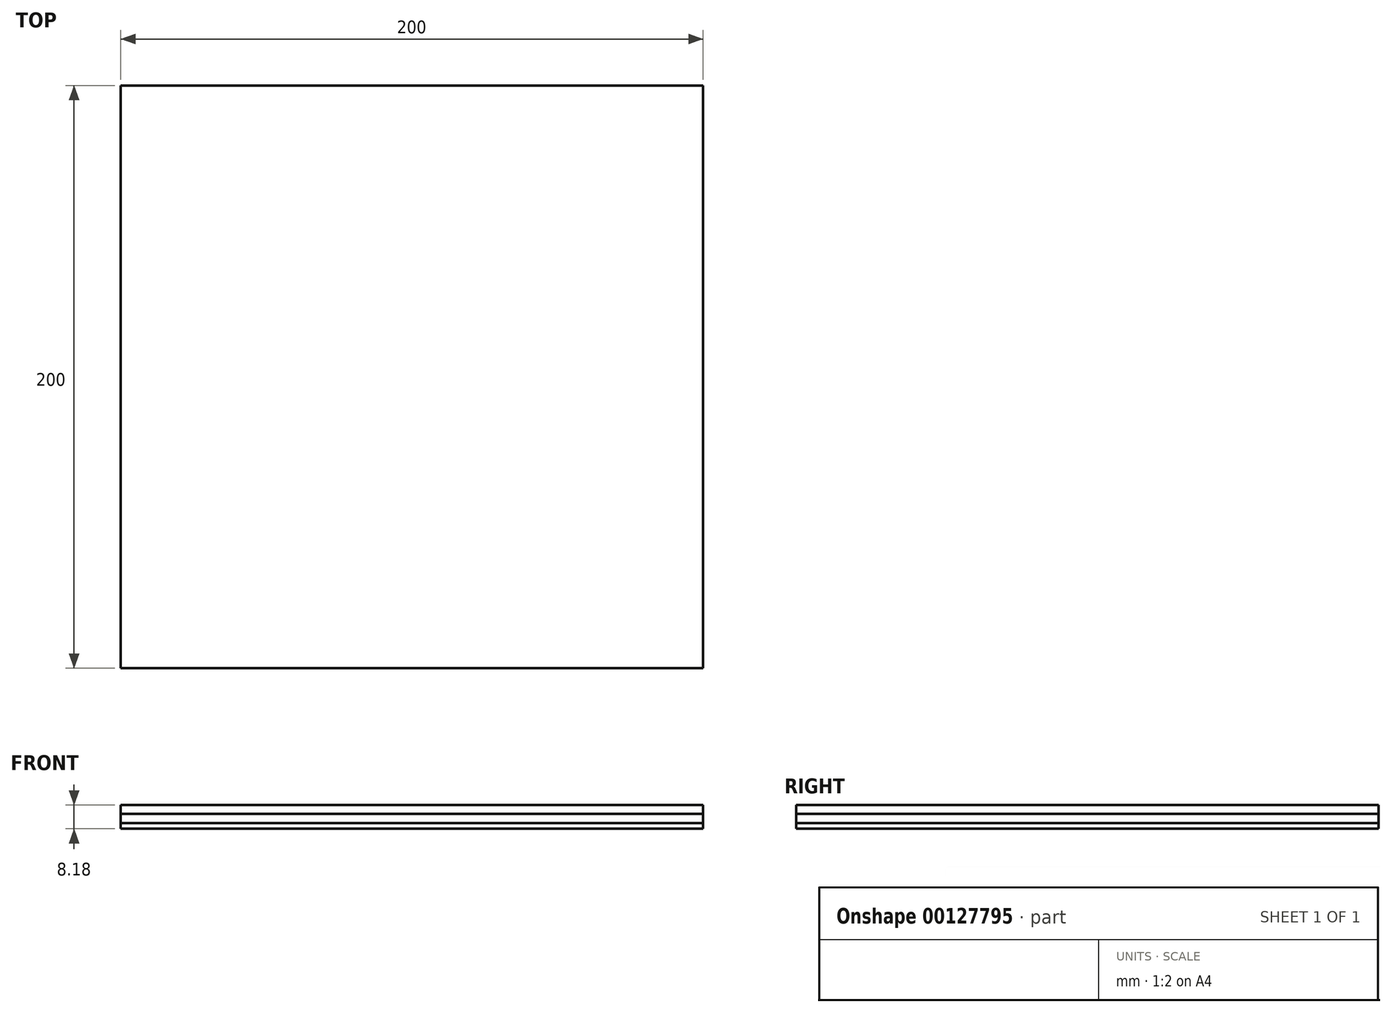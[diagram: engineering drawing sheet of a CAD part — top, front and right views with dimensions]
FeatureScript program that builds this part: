
annotation { "Feature Type Name" : "Feature", "Feature Type Description" : "" }
export const myFeature = defineFeature(function(context is Context, id is Id, definition is map)
    precondition{}
    {
        {
            var Q0;
            Q0=qCreatedBy(makeId("Top.planeOp"),FACE);
            var sketch = newSketch(context, id + "F0", { "sketchPlane" : qUnion([Q0])});
            skLineSegment(sketch, "E0.bottom", {"start": v(100, -100) * mm, "end": v(-100, -100) * mm});
            skLineSegment(sketch, "E0.top", {"start": v(100, 100) * mm, "end": v(-100, 100) * mm});
            skLineSegment(sketch, "E0.left", {"start": v(100, -100) * mm, "end": v(100, 100) * mm});
            skLineSegment(sketch, "E0.right", {"start": v(-100, -100) * mm, "end": v(-100, 100) * mm});
            skPoint(sketch, "E0.middle", {"position": v(0, 0) * mm});
            skSolve(sketch);
        }
        {
            var Q0;
            Q0 = qSketchRegion(id + "F0", true);
            extrude(context, id + "F1", {"entities" : qUnion([Q0]), "endBound" : BoundingType.SYMMETRIC, "depth" : 3.17 * mm});
        }
        {
            var Q0;
            Q0=makeQuery(id+"F1.opExtrude","CAP_FACE",FACE,{"disambiguationData":[OSD([sQuery(id+"F0.wireOp",EDGE,"E0.bottom"),sQuery(id+"F0.wireOp",EDGE,"E0.top"),sQuery(id+"F0.wireOp",EDGE,"E0.left"),sQuery(id+"F0.wireOp",EDGE,"E0.right")])],"isStart":false});
            var sketch = newSketch(context, id + "F2", { "sketchPlane" : qUnion([Q0])});
            skCircle(sketch, "E1", {"center": v(-90, -140) * mm, "radius": 2.5 * mm});
            skCircle(sketch, "E2", {"center": v(-90, 140) * mm, "radius": 2.5 * mm});
            skLineSegment(sketch, "E3", {"start": v(-46.85, 0) * mm, "end": v(0, 0) * mm, "construction": true});
            skLineSegment(sketch, "E4", {"start": v(0, 0) * mm, "end": v(0, 84.57) * mm, "construction": true});
            skCircle(sketch, "E5.MirrorC", {"center": v(90, 140) * mm, "radius": 2.5 * mm});
            skCircle(sketch, "E6.MirrorC", {"center": v(90, -140) * mm, "radius": 2.5 * mm});
            skSolve(sketch);
        }
        {
            var Q0;
            Q0 = qSketchRegion(id + "F2", true);
            extrude(context, id + "F3", {"entities" : qUnion([Q0]), "operationType" : NewBodyOperationType.REMOVE, "endBound" : BoundingType.THROUGH_ALL, "oppositeDirection" : true, "depth" : 25 * mm});
        }
        {
            var Q0;
            Q0=makeQuery(id+"F1.opExtrude","CAP_FACE",FACE,{"disambiguationData":[OSD([sQuery(id+"F0.wireOp",EDGE,"E0.bottom"),sQuery(id+"F0.wireOp",EDGE,"E0.top"),sQuery(id+"F0.wireOp",EDGE,"E0.left"),sQuery(id+"F0.wireOp",EDGE,"E0.right")])],"isStart":true});
            var sketch = newSketch(context, id + "F4", { "sketchPlane" : qUnion([Q0])});
            skLineSegment(sketch, "E7.bottom", {"start": v(100, -100) * mm, "end": v(-100, -100) * mm});
            skLineSegment(sketch, "E7.top", {"start": v(100, 100) * mm, "end": v(-100, 100) * mm});
            skLineSegment(sketch, "E7.left", {"start": v(100, -100) * mm, "end": v(100, 100) * mm});
            skLineSegment(sketch, "E7.right", {"start": v(-100, -100) * mm, "end": v(-100, 100) * mm});
            skPoint(sketch, "E7.middle", {"position": v(0, 0) * mm});
            skSolve(sketch);
        }
        {
            var Q0;
            Q0 = qSketchRegion(id + "F4", true);
            extrude(context, id + "F5", {"entities" : qUnion([Q0]), "depth" : 2 * mm});
        }
        {
            var Q0;
            Q0=makeQuery(id+"F1.opExtrude","CAP_FACE",FACE,{"disambiguationData":[OSD([sQuery(id+"F0.wireOp",EDGE,"E0.bottom"),sQuery(id+"F0.wireOp",EDGE,"E0.top"),sQuery(id+"F0.wireOp",EDGE,"E0.left"),sQuery(id+"F0.wireOp",EDGE,"E0.right")])],"isStart":false});
            var sketch = newSketch(context, id + "F6", { "sketchPlane" : qUnion([Q0])});
            skLineSegment(sketch, "E8.0.0", {"start": v(-100, -100) * mm, "end": v(100, -100) * mm});
            skLineSegment(sketch, "E8.0.1", {"start": v(100, -100) * mm, "end": v(100, 100) * mm});
            skLineSegment(sketch, "E8.0.2", {"start": v(100, 100) * mm, "end": v(-100, 100) * mm});
            skLineSegment(sketch, "E8.0.3", {"start": v(-100, 100) * mm, "end": v(-100, -100) * mm});
            skSolve(sketch);
        }
        {
            var Q0;
            Q0 = qSketchRegion(id + "F6", true);
            extrude(context, id + "F7", {"entities" : qUnion([Q0]), "depth" : 3 * mm});
        }
    });
